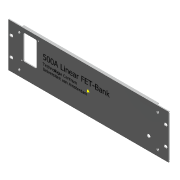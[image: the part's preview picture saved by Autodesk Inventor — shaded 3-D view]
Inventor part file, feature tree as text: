
AUTODESK INVENTOR PART (.ipt)
format: ipt  version: 2016 SP2 (Build 200236200, 236)  size: 223,744 bytes
history: native  units: in
note: dims shown in document units (in); Inventor stores cm internally (conversion verified against a paired STEP export)
features: sketch x4, reference x4, extrude x2, fillet x1, hole x1
ambient origin geometry x8: Origin, YZ Plane, XZ Plane, XY Plane, X Axis, Y Axis, Z Axis, Center Point
bodies: Solid1 (feature_tree)
feature tree (12):
  sketch  "Sketch1"  dims[d8=0.1969in d9=0.1969in d10=0.1969in]
  extrude  "Extrusion2"  Depth=0.1969in
  fillet  "Fillet2"  Radius=0.1969in
  extrude  "Extrusion3"  Depth=0.3937in TaperAngle=0.0deg
  hole  "Hole2"  [1 undecoded]
  sketch  "Sketch3"  dims[d11=0.1969in d12=0.3937in d13=0.0in]
  reference  "Reference3"
  reference  "Reference4"
  sketch  "Sketch4"  dims[d14=0.1575in d15=2.3622in]
  sketch  "Sketch5"  dims[d16=1.5748in d24=0.3937in d25=0.3543in d26=0.3937in d27=0.0in d30=0.126in d31=0.2362in d32=0.1575in d33=0.0787in d34=90.0deg d35=0.315in d36=0.8108in]
  reference  "Reference5"
  reference  "Reference6"
note: 1 required parameter value undecoded (feature->parameter linkage not recoverable at this tier; creation-order binding heuristic only, values carry confidence <= 0.55)
